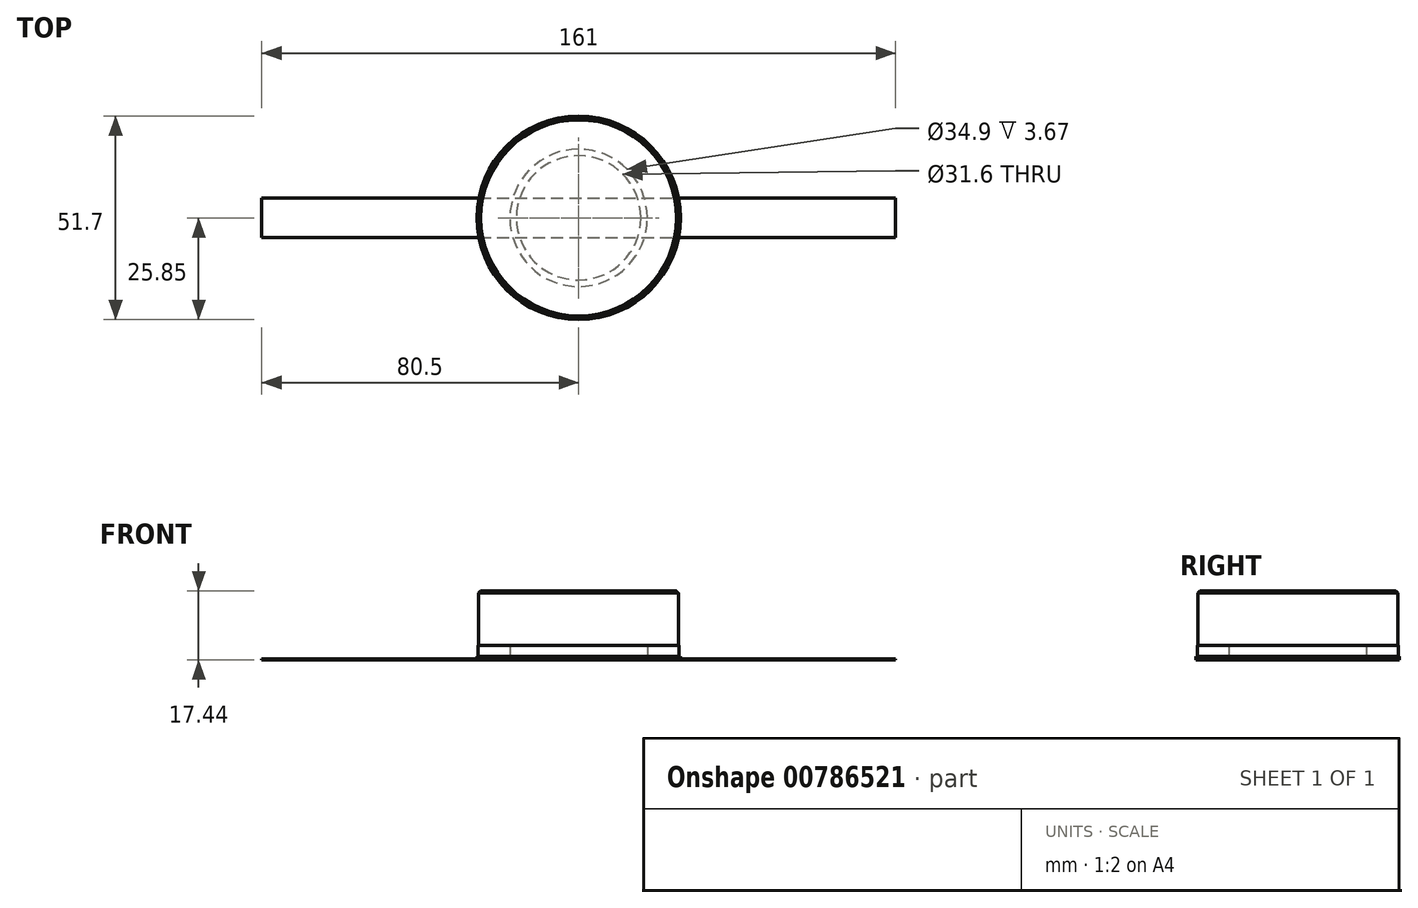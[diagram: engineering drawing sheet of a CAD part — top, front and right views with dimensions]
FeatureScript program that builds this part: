
annotation { "Feature Type Name" : "Feature", "Feature Type Description" : "" }
export const myFeature = defineFeature(function(context is Context, id is Id, definition is map)
    precondition{}
    {
        {
            var Q0;
            Q0=qCreatedBy(makeId("Top.planeOp"),FACE);
            var sketch = newSketch(context, id + "F0", { "sketchPlane" : qUnion([Q0])});
            skCircle(sketch, "E0", {"center": v(0, 0) * mm, "radius": 25.4 * mm});
            skSolve(sketch);
        }
        {
            var Q0;
            Q0 = qSketchRegion(id + "F0", true);
            extrude(context, id + "F1", {"entities" : qUnion([Q0]), "depth" : 17.44 * mm, "offsetDistance" : 25 * mm});
        }
        {
            var Q0;
            Q0=qCreatedBy(makeId("Top.planeOp"),FACE);
            var sketch = newSketch(context, id + "F2", { "sketchPlane" : qUnion([Q0])});
            skCircle(sketch, "E1", {"center": v(0, 0) * mm, "radius": 15.8 * mm});
            skCircle(sketch, "E2", {"center": v(0, 0) * mm, "radius": 25.85 * mm});
            skSolve(sketch);
        }
        {
            var Q0;
            Q0 = qSketchRegion(id + "F2", true);
            extrude(context, id + "F3", {"entities" : qUnion([Q0]), "depth" : 0.8 * mm, "offsetDistance" : 25 * mm});
        }
        {
            var Q0;
            Q0=qCreatedBy(makeId("Top.planeOp"),FACE);
            var sketch = newSketch(context, id + "F4", { "sketchPlane" : qUnion([Q0])});
            skCircle(sketch, "E3", {"center": v(0, 0) * mm, "radius": 17.45 * mm});
            skCircle(sketch, "E4", {"center": v(0, 0) * mm, "radius": 25.5 * mm});
            skSolve(sketch);
        }
        {
            var Q0;
            Q0 = qSketchRegion(id + "F4", true);
            extrude(context, id + "F5", {"entities" : qUnion([Q0]), "depth" : 3.67 * mm, "offsetDistance" : 25 * mm});
        }
        {
            var Q0;
            Q0=qCreatedBy(makeId("Top.planeOp"),FACE);
            var sketch = newSketch(context, id + "F6", { "sketchPlane" : qUnion([Q0])});
            skCircle(sketch, "E5", {"center": v(0, 0) * mm, "radius": 25.83 * mm});
            skSolve(sketch);
        }
        {
            var Q0;
            Q0 = qSketchRegion(id + "F6", true);
            extrude(context, id + "F7", {"entities" : qUnion([Q0]), "depth" : 0.28 * mm, "offsetDistance" : 25 * mm});
        }
        {
            var Q0;
            Q0=makeQuery(id+"F1.opExtrude","CAP_EDGE",EDGE,{"disambiguationData":[OSD([sQuery(id+"F0.wireOp",EDGE,"E0")])],"isStart":false});
            var Q1;
            Q1=makeQuery(id+"F1.opExtrude","CAP_EDGE",EDGE,{"disambiguationData":[OSD([sQuery(id+"F0.wireOp",EDGE,"E0")])],"isStart":true});
            chamfer(context, id + "F8", {"entities" : qUnion([Q0, Q1]), "width" : 0.5 * mm, "tangentPropagation" : true});
        }
        {
            var Q0;
            Q0=qCreatedBy(makeId("Top.planeOp"),FACE);
            var sketch = newSketch(context, id + "F9", { "sketchPlane" : qUnion([Q0])});
            skLineSegment(sketch, "E6.bottom", {"start": v(-80.5, 5) * mm, "end": v(80.5, 5) * mm});
            skLineSegment(sketch, "E6.top", {"start": v(-80.5, -5) * mm, "end": v(80.5, -5) * mm});
            skLineSegment(sketch, "E6.left", {"start": v(-80.5, 5) * mm, "end": v(-80.5, -5) * mm});
            skLineSegment(sketch, "E6.right", {"start": v(80.5, 5) * mm, "end": v(80.5, -5) * mm});
            skPoint(sketch, "E6.middle", {"position": v(0, 0) * mm});
            skSolve(sketch);
        }
        {
            var Q0;
            Q0 = qSketchRegion(id + "F9", true);
            extrude(context, id + "F10", {"entities" : qUnion([Q0]), "depth" : 0.25 * mm, "offsetDistance" : 25 * mm});
        }
    });
